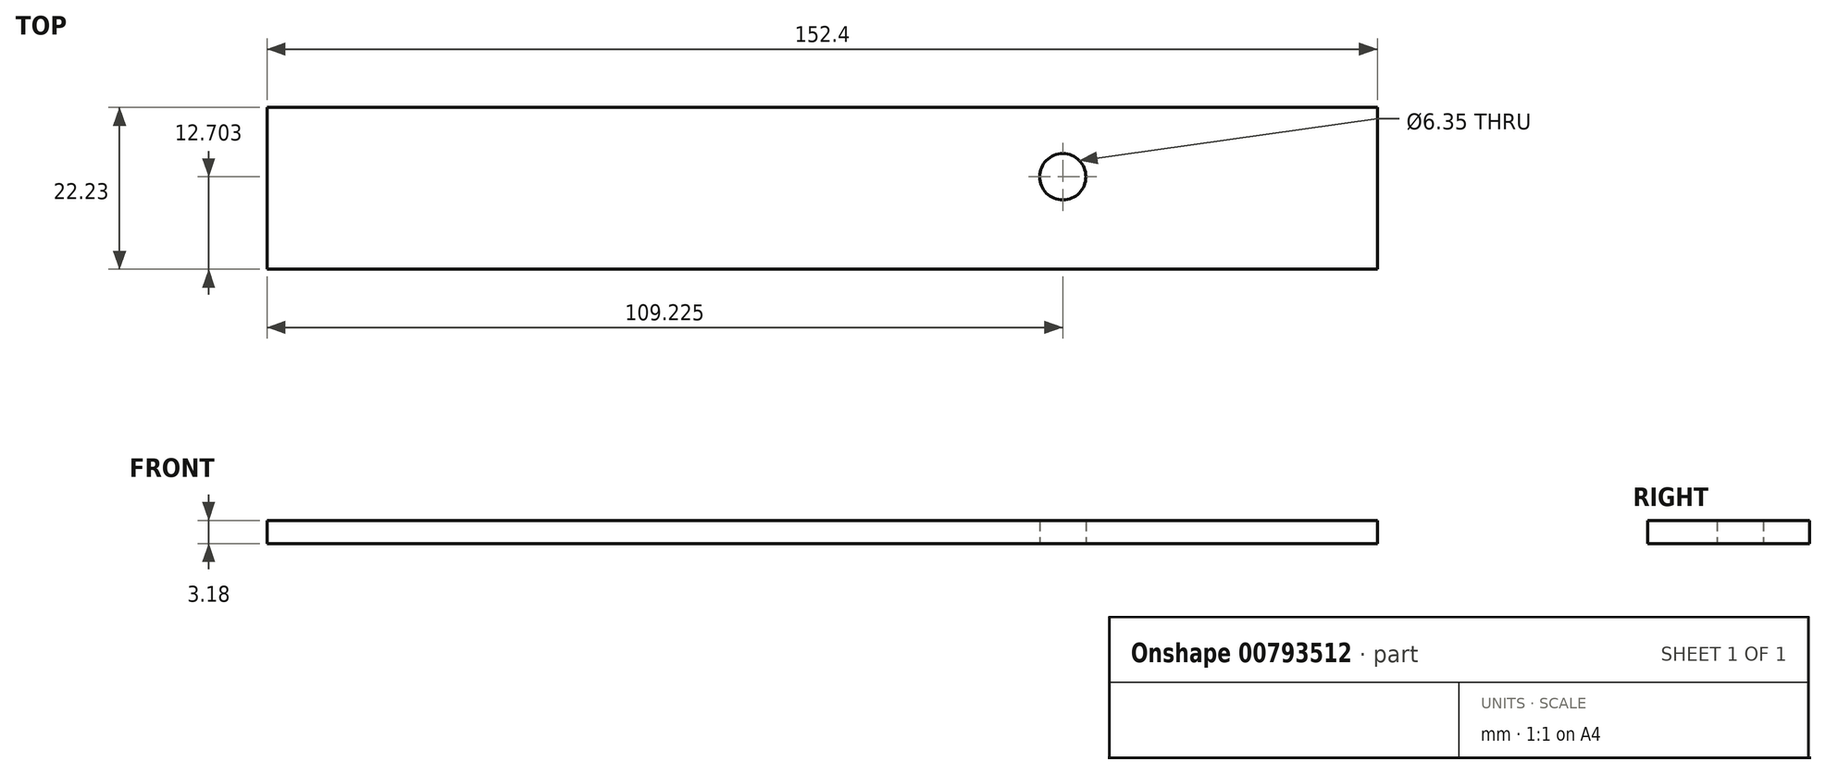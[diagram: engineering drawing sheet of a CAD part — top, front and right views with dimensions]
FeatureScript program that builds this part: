
annotation { "Feature Type Name" : "Feature", "Feature Type Description" : "" }
export const myFeature = defineFeature(function(context is Context, id is Id, definition is map)
    precondition{}
    {
        {
            var Q0;
            Q0=qCreatedBy(makeId("Top.planeOp"),FACE);
            var sketch = newSketch(context, id + "F0", { "sketchPlane" : qUnion([Q0])});
            skLineSegment(sketch, "E0.bottom", {"start": v(-83.24, 4.33) * mm, "end": v(69.16, 4.33) * mm});
            skLineSegment(sketch, "E0.top", {"start": v(-83.24, -17.9) * mm, "end": v(69.16, -17.9) * mm});
            skLineSegment(sketch, "E0.left", {"start": v(-83.24, 4.33) * mm, "end": v(-83.24, -17.9) * mm});
            skLineSegment(sketch, "E0.right", {"start": v(69.16, 4.33) * mm, "end": v(69.16, -17.9) * mm});
            skCircle(sketch, "E1", {"center": v(25.98, -5.2) * mm, "radius": 3.18 * mm});
            skSolve(sketch);
        }
        {
            var Q0;
            Q0=qSketchRegion(id+"F0",true);
            extrude(context, id + "F1", {"entities" : qUnion([Q0]), "depth" : 3.17 * mm, "offsetDistance" : 25.4 * mm});
        }
    });
